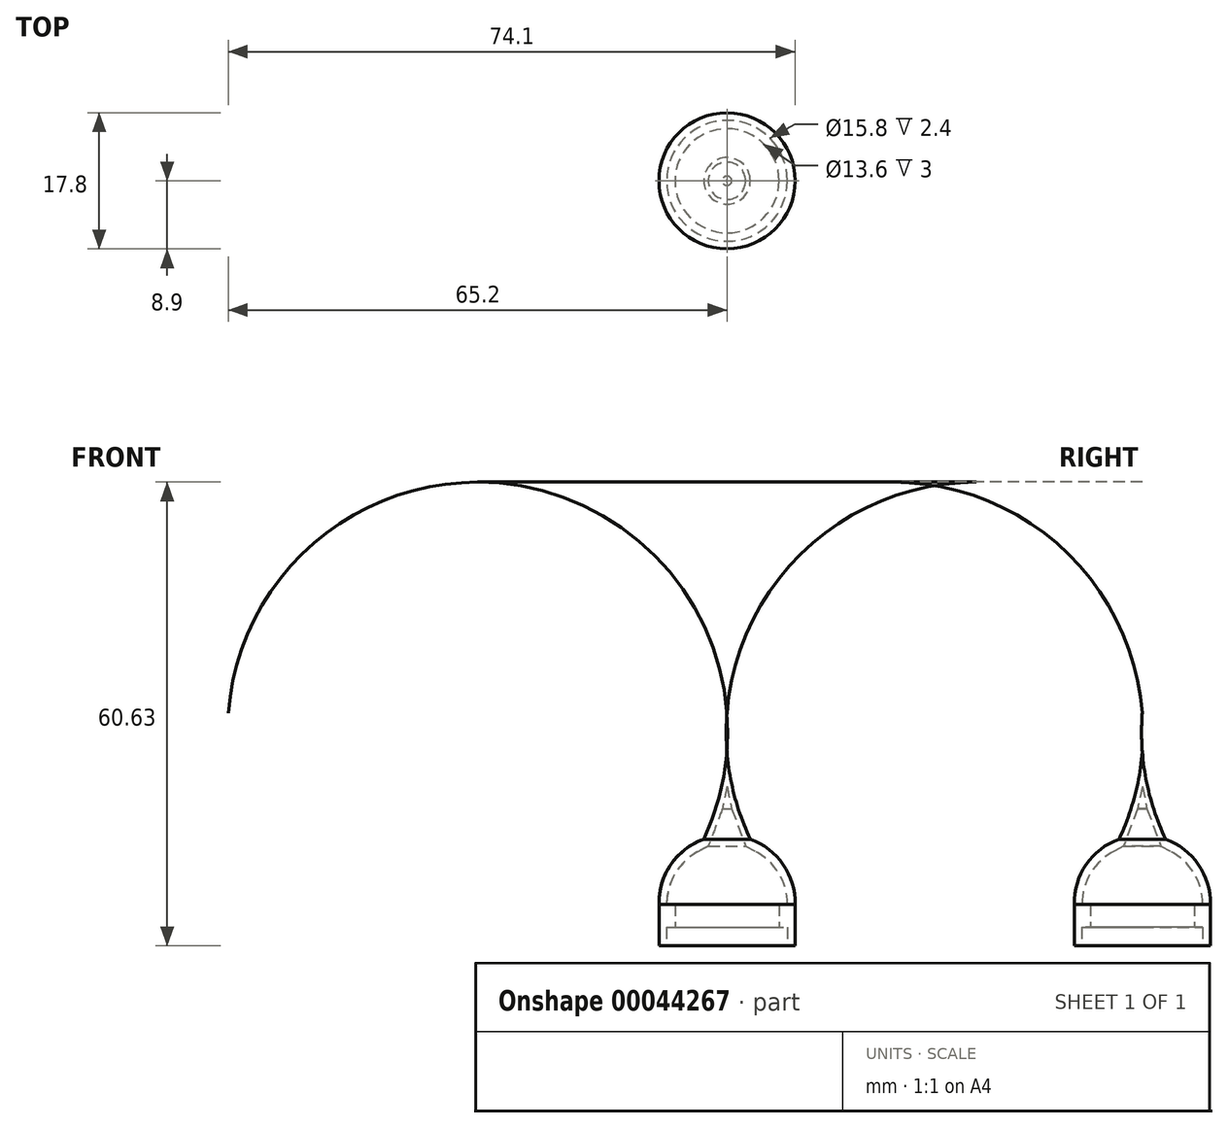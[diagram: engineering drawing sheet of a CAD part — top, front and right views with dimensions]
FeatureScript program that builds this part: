
annotation { "Feature Type Name" : "Feature", "Feature Type Description" : "" }
export const myFeature = defineFeature(function(context is Context, id is Id, definition is map)
    precondition{}
    {
        {
            var Q0;
            Q0=qCreatedBy(makeId("Top.planeOp"),FACE);
            var sketch = newSketch(context, id + "F0", { "sketchPlane" : qUnion([Q0])});
            skLineSegment(sketch, "E0", {"start": v(-17.52, 0) * mm, "end": v(42.68, 0) * mm, "construction": true});
            skLineSegment(sketch, "E1", {"start": v(0, 0) * mm, "end": v(0, 7.9) * mm, "construction": true});
            skLineSegment(sketch, "E2", {"start": v(0, 7.9) * mm, "end": v(2.4, 7.9) * mm});
            skLineSegment(sketch, "E3", {"start": v(2.4, 6.8) * mm, "end": v(2.4, 7.9) * mm});
            skLineSegment(sketch, "E4", {"start": v(2.4, 6.8) * mm, "end": v(5.4, 6.8) * mm});
            skLineSegment(sketch, "E5", {"start": v(0, 7.9) * mm, "end": v(0, 8.9) * mm});
            skLineSegment(sketch, "E6", {"start": v(5.4, 6.8) * mm, "end": v(5.4, 7.9) * mm});
            skLineSegment(sketch, "E7", {"start": v(0, 8.9) * mm, "end": v(5.4, 8.9) * mm});
            skLineSegment(sketch, "E8", {"start": v(2.4, 7.9) * mm, "end": v(5.4, 7.9) * mm, "construction": true});
            skArc(sketch, "E9", {"start": v(5.4, 7.9) * mm, "mid": v(9.52, 6.74) * mm, "end": v(12.43, 3.61) * mm});
            skLineSegment(sketch, "E10", {"start": v(5.4, 8.9) * mm, "end": v(5.4, 0) * mm, "construction": true});
            skLineSegment(sketch, "E11", {"start": v(5.4, 8.9) * mm, "end": v(5.4, 47.7) * mm, "construction": true});
            skArc(sketch, "E12", {"start": v(13.95, 3.04) * mm, "mid": v(10.62, 7.34) * mm, "end": v(5.4, 8.9) * mm});
            skArc(sketch, "E13.trimOffspring", {"start": v(13.95, 3.04) * mm, "mid": v(19.54, 1) * mm, "end": v(25.4, 0) * mm});
            skLineSegment(sketch, "E14", {"start": v(12.43, 3.61) * mm, "end": v(13.03, 2.44) * mm});
            skLineSegment(sketch, "E15", {"start": v(13.03, 2.44) * mm, "end": v(17.93, 0.61) * mm});
            skLineSegment(sketch, "E16", {"start": v(17.93, 0.61) * mm, "end": v(20.87, 0) * mm});
            skLineSegment(sketch, "E17", {"start": v(20.87, 0) * mm, "end": v(25.4, 0) * mm});
            skSolve(sketch);
        }
        {
            var Q0;
            Q0=makeQuery(id+"F0.imprint","IMPRINT",FACE,{"disambiguationData":[TD([[makeQuery(id+"F0.imprint","IMPRINT",EDGE,{"derivedFrom":sQuery(id+"F0.wireOp",EDGE,"E2")}),1.0]])]});
            var Q1;
            Q1=sQuery(id+"F0.wireOp",EDGE,"E0");
            revolve(context, id + "F1", {"entities" : qUnion([Q0]), "axis" : qUnion([Q1]), "revolveType" : RevolveType.FULL});
        }
        {
            var Q0;
            Q0=qCreatedBy(makeId("Front.planeOp"),FACE);
            var sketch = newSketch(context, id + "F2", { "sketchPlane" : qUnion([Q0])});
            skCircle(sketch, "E18", {"center": v(0, 0) * mm, "radius": 9.63 * mm, "construction": true});
            skSolve(sketch);
        }
        {
            var Q0;
            Q0=makeQuery(id+"F1.opRevolve","SWEPT_BODY",BODY,{"disambiguationData":[OSD([sQuery(id+"F0.wireOp",EDGE,"E2"),sQuery(id+"F0.wireOp",EDGE,"E3"),sQuery(id+"F0.wireOp",EDGE,"E4"),sQuery(id+"F0.wireOp",EDGE,"E5"),sQuery(id+"F0.wireOp",EDGE,"E6"),sQuery(id+"F0.wireOp",EDGE,"E7"),sQuery(id+"F0.wireOp",EDGE,"E9"),sQuery(id+"F0.wireOp",EDGE,"E12"),sQuery(id+"F0.wireOp",EDGE,"E13.trimOffspring"),sQuery(id+"F0.wireOp",EDGE,"E14"),sQuery(id+"F0.wireOp",EDGE,"E15"),sQuery(id+"F0.wireOp",EDGE,"E16"),sQuery(id+"F0.wireOp",EDGE,"E17")])]});
            var Q1;
            Q1=sQuery(id+"F2.wireOp",EDGE,"E18");
            transform(context, id + "F3", {"entities" : qUnion([Q0]), "transformType" : TransformType.ROTATION, "transformAxis" : qUnion([Q1]), "angle" : 90 * degree, "makeCopy" : false});
        }
    });
